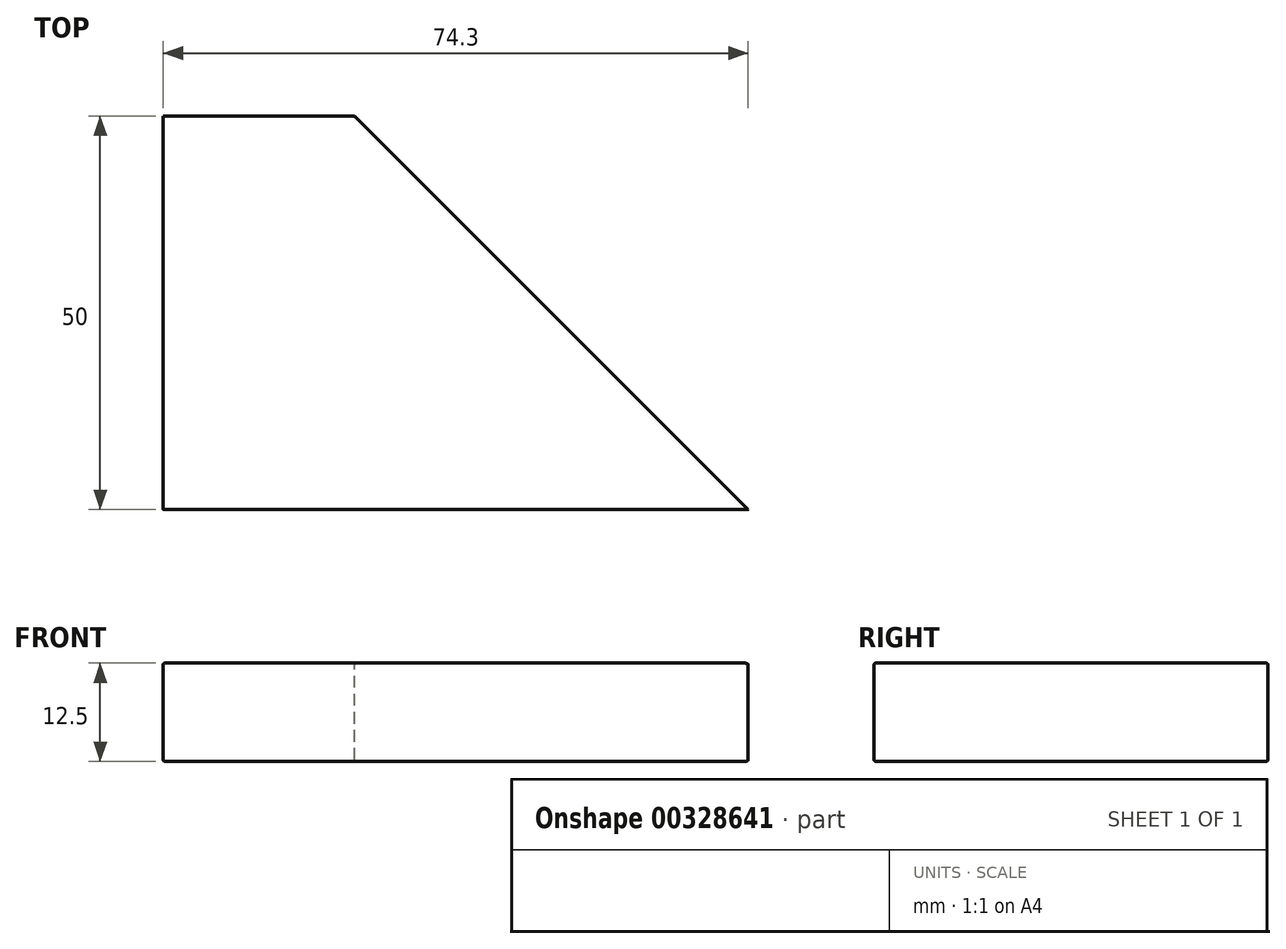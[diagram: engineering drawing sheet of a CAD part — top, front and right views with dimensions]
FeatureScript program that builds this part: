
annotation { "Feature Type Name" : "Feature", "Feature Type Description" : "" }
export const myFeature = defineFeature(function(context is Context, id is Id, definition is map)
    precondition{}
    {
        {
            var Q0;
            Q0=qCreatedBy(makeId("Top.planeOp"),FACE);
            var sketch = newSketch(context, id + "F0", { "sketchPlane" : qUnion([Q0])});
            skLineSegment(sketch, "E0.bottom", {"start": v(0, 0) * mm, "end": v(74.3, 0) * mm});
            skLineSegment(sketch, "E0.top", {"start": v(0, 50) * mm, "end": v(24.3, 50) * mm});
            skLineSegment(sketch, "E0.left", {"start": v(0, 0) * mm, "end": v(0, 50) * mm});
            skLineSegment(sketch, "E1", {"start": v(74.3, 0) * mm, "end": v(24.3, 50) * mm});
            skSolve(sketch);
        }
        {
            var Q0;
            Q0=qSketchRegion(id+"F0",true);
            extrude(context, id + "F1", {"entities" : qUnion([Q0]), "oppositeDirection" : true, "depth" : 12.5 * mm});
        }
        {
            var Q0;
            Q0=makeQuery(id+"F1.opExtrude","CAP_FACE",FACE,{"disambiguationData":[OSD([sQuery(id+"F0.wireOp",EDGE,"E0.bottom"),sQuery(id+"F0.wireOp",EDGE,"E0.top"),sQuery(id+"F0.wireOp",EDGE,"E0.left"),sQuery(id+"F0.wireOp",EDGE,"E0.right")])],"isStart":true});
            var Q1;
            Q1=makeQuery(id+"F1.opExtrude","CAP_FACE",FACE,{"disambiguationData":[OSD([sQuery(id+"F0.wireOp",EDGE,"E0.bottom"),sQuery(id+"F0.wireOp",EDGE,"E0.top"),sQuery(id+"F0.wireOp",EDGE,"E0.left"),sQuery(id+"F0.wireOp",EDGE,"E0.right")])],"isStart":false});
            fillet(context, id + "F2", {"entities" : qUnion([Q0, Q1]), "radius" : .2 * mm, "tangentPropagation" : true, "allowEdgeOverflow" : false});
        }
    });
